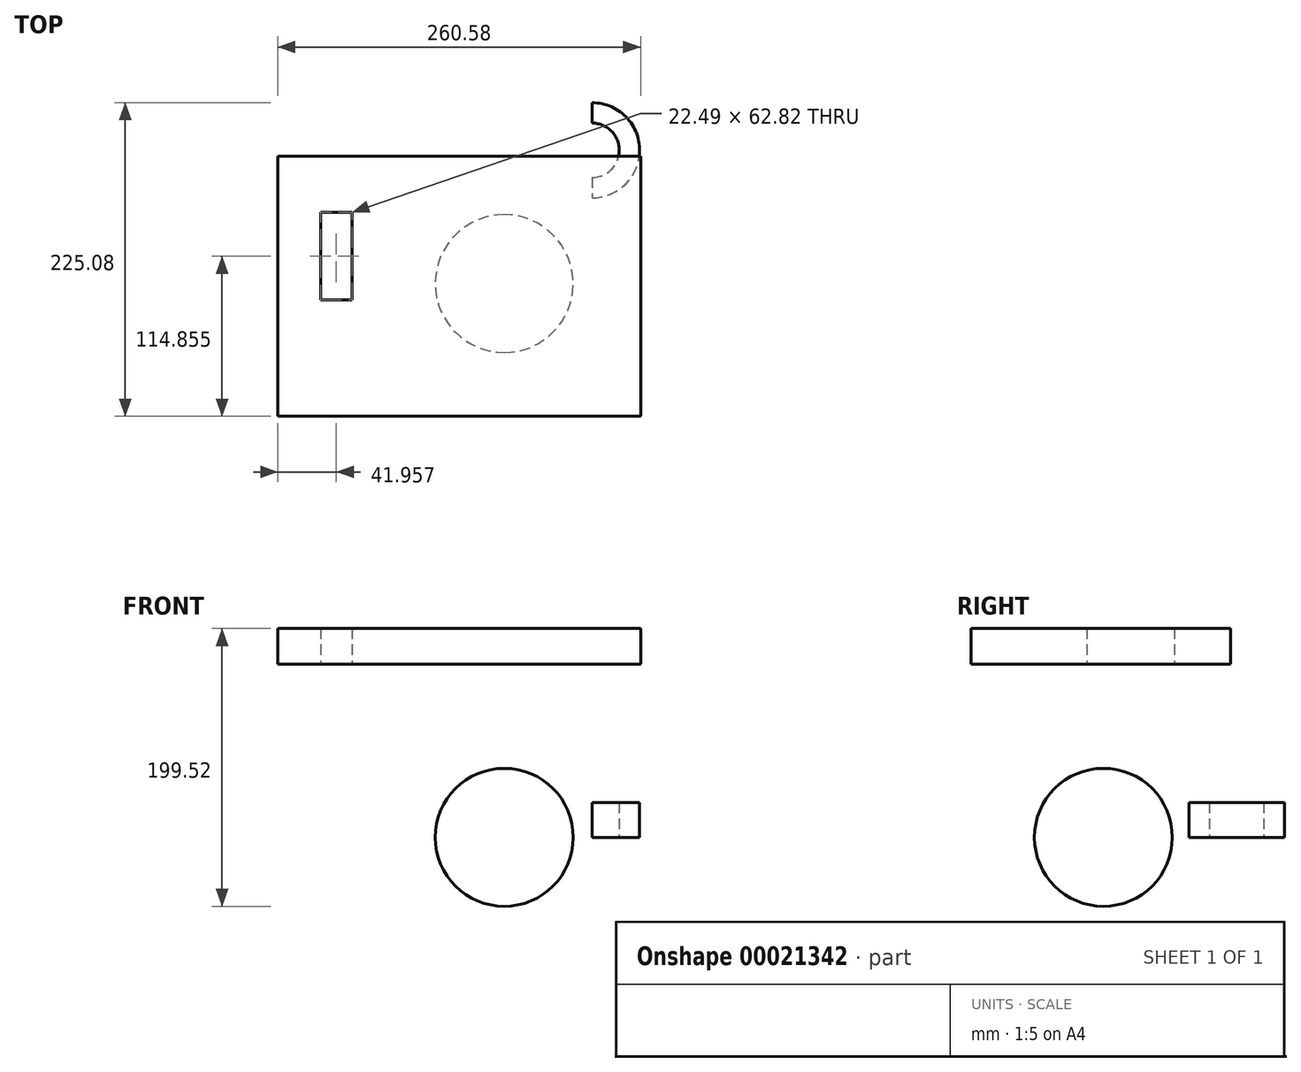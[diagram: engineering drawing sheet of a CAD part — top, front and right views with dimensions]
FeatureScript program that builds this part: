
annotation { "Feature Type Name" : "Feature", "Feature Type Description" : "" }
export const myFeature = defineFeature(function(context is Context, id is Id, definition is map)
    precondition{}
    {
        {
            var Q0;
            Q0=qCreatedBy(makeId("Top.planeOp"),FACE);
            var sketch = newSketch(context, id + "F0", { "sketchPlane" : qUnion([Q0])});
            skArc(sketch, "E0", {"start": v(0, 49.52) * mm, "mid": v(-49.52, 0) * mm, "end": v(0, -49.52) * mm});
            skLineSegment(sketch, "E1", {"start": v(0, -49.52) * mm, "end": v(0, 49.52) * mm});
            skSolve(sketch);
        }
        {
            var Q0;
            Q0=makeQuery(id+"F0.imprint","IMPRINT",FACE,{"disambiguationData":[TD([[makeQuery(id+"F0.imprint","IMPRINT",EDGE,{"derivedFrom":sQuery(id+"F0.wireOp",EDGE,"E0")}),1.0]])]});
            var Q1;
            Q1=sQuery(id+"F0.wireOp",EDGE,"E1");
            revolve(context, id + "F1", {"entities" : qUnion([Q0]), "axis" : qUnion([Q1]), "revolveType" : RevolveType.FULL});
        }
        {
            var Q0;
            Q0=qCreatedBy(makeId("Top.planeOp"),FACE);
            cPlane(context, id + "F2", {"entities" : qUnion([Q0]), "cplaneType" : CPlaneType.OFFSET, "offset" : 150 * mm, "width" : 152.4 * mm, "height" : 152.4 * mm});
        }
        {
            var Q0;
            Q0=qCreatedBy(id+"F2.planeOp",FACE);
            var sketch = newSketch(context, id + "F3", { "sketchPlane" : qUnion([Q0])});
            skLineSegment(sketch, "E2.bottom", {"start": v(97.98, 91.49) * mm, "end": v(-162.6, 91.49) * mm});
            skLineSegment(sketch, "E2.top", {"start": v(97.98, -95.17) * mm, "end": v(-162.6, -95.17) * mm});
            skLineSegment(sketch, "E2.left", {"start": v(97.98, 91.49) * mm, "end": v(97.98, -95.17) * mm});
            skLineSegment(sketch, "E2.right", {"start": v(-162.6, 91.49) * mm, "end": v(-162.6, -95.17) * mm});
            skSolve(sketch);
        }
        {
            var Q0;
            Q0=makeQuery(id+"F3.imprint","IMPRINT",FACE,{"disambiguationData":[TD([[makeQuery(id+"F3.imprint","IMPRINT",EDGE,{"derivedFrom":sQuery(id+"F3.wireOp",EDGE,"E2.bottom")}),1.0]])]});
            extrude(context, id + "F4", {"entities" : qUnion([Q0]), "oppositeDirection" : true, "depth" : 25.54 * mm});
        }
        {
            var Q0;
            Q0=qCreatedBy(makeId("Top.planeOp"),FACE);
            var sketch = newSketch(context, id + "F5", { "sketchPlane" : qUnion([Q0])});
            skCircle(sketch, "E3", {"center": v(63.02, 95.74) * mm, "radius": 34.18 * mm});
            skCircle(sketch, "E4", {"center": v(63.02, 95.74) * mm, "radius": 19.56 * mm});
            skLineSegment(sketch, "E5", {"start": v(63.02, 129.91) * mm, "end": v(63.02, 115.3) * mm});
            skLineSegment(sketch, "E6", {"start": v(63.02, 76.17) * mm, "end": v(63.02, 61.56) * mm});
            skSolve(sketch);
        }
        {
            var Q0;
            {var subQ1=sQuery(id+"F5.wireOp",EDGE,"E5");Q0=makeQuery(id+"F5.imprint","IMPRINT",FACE,{"disambiguationData":[TD([[makeQuery(id+"F5.imprint","IMPRINT",EDGE,{"derivedFrom":subQ1}),1.0]])]});}
            extrude(context, id + "F6", {"entities" : qUnion([Q0]), "depth" : 25 * mm});
        }
        {
            var Q0;
            Q0=makeQuery(id+"F4.opExtrude","CAP_FACE",FACE,{"disambiguationData":[OSD([sQuery(id+"F3.wireOp",EDGE,"E2.bottom"),sQuery(id+"F3.wireOp",EDGE,"E2.top"),sQuery(id+"F3.wireOp",EDGE,"E2.left"),sQuery(id+"F3.wireOp",EDGE,"E2.right")])],"isStart":false});
            var sketch = newSketch(context, id + "F7", { "sketchPlane" : qUnion([Q0])});
            skLineSegment(sketch, "E7.bottom", {"start": v(-109.4, 11.73) * mm, "end": v(-131.89, 11.73) * mm});
            skLineSegment(sketch, "E7.top", {"start": v(-109.4, -51.1) * mm, "end": v(-131.89, -51.1) * mm});
            skLineSegment(sketch, "E7.left", {"start": v(-109.4, 11.73) * mm, "end": v(-109.4, -51.1) * mm});
            skLineSegment(sketch, "E7.right", {"start": v(-131.89, 11.73) * mm, "end": v(-131.89, -51.1) * mm});
            skSolve(sketch);
        }
        {
            var Q0;
            Q0=makeQuery(id+"F7.imprint","IMPRINT",FACE,{"disambiguationData":[TD([[makeQuery(id+"F7.imprint","IMPRINT",EDGE,{"derivedFrom":sQuery(id+"F7.wireOp",EDGE,"E7.bottom")}),1.0]])]});
            extrude(context, id + "F8", {"entities" : qUnion([Q0]), "operationType" : NewBodyOperationType.REMOVE, "endBound" : BoundingType.UP_TO_NEXT, "oppositeDirection" : true, "depth" : 25 * mm});
        }
    });
